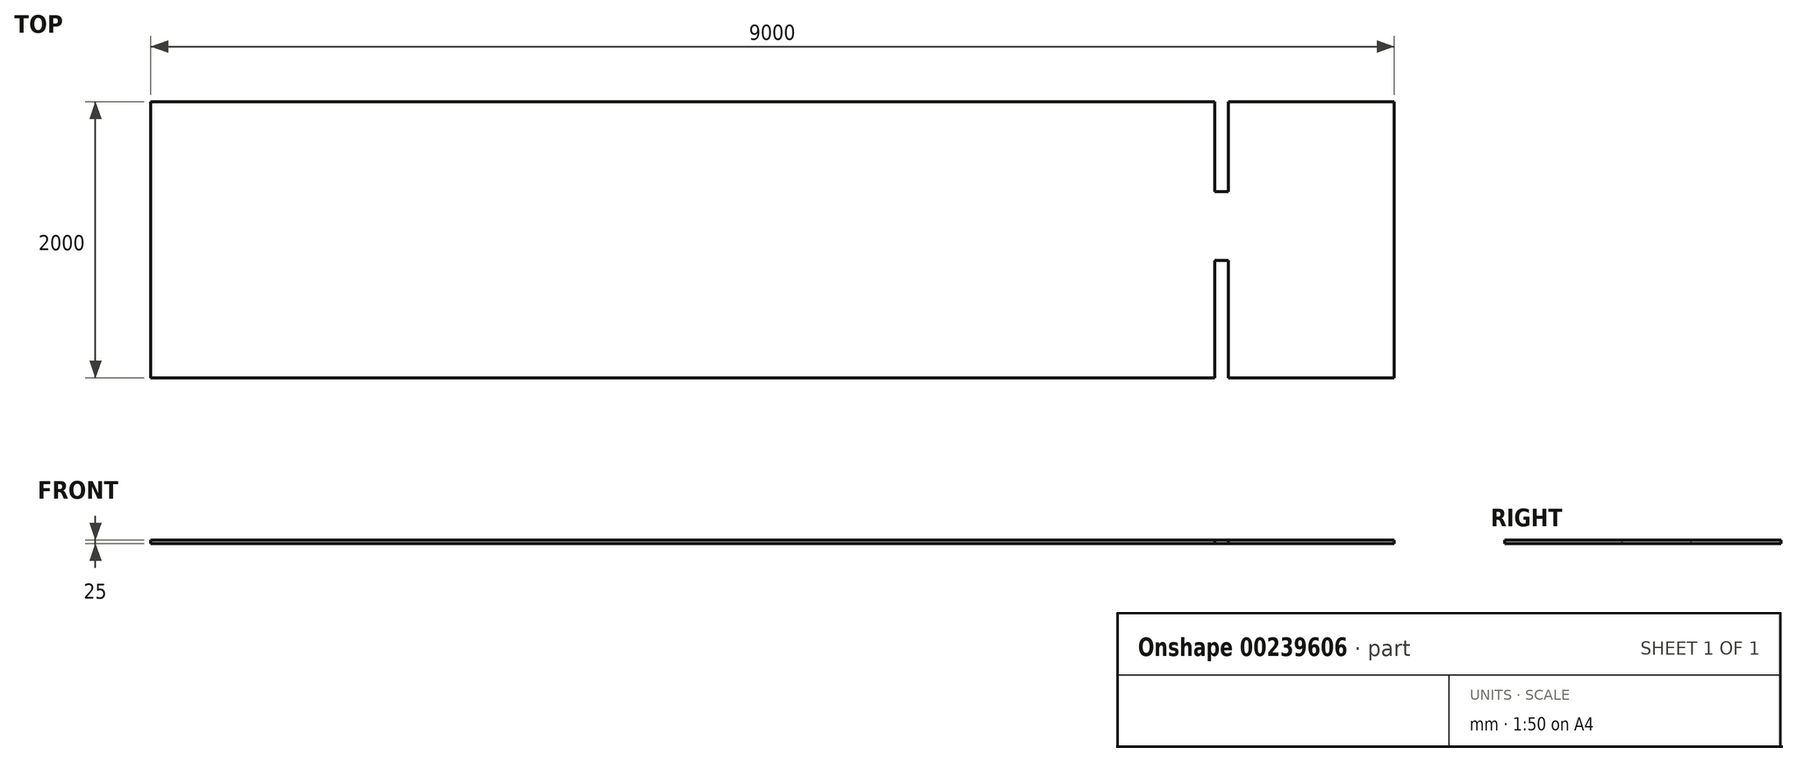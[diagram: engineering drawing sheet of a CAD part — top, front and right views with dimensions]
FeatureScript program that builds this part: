
annotation { "Feature Type Name" : "Feature", "Feature Type Description" : "" }
export const myFeature = defineFeature(function(context is Context, id is Id, definition is map)
    precondition{}
    {
        {
            var Q0;
            Q0=qCreatedBy(makeId("Top.planeOp"),FACE);
            var sketch = newSketch(context, id + "F0", { "sketchPlane" : qUnion([Q0])});
            skLineSegment(sketch, "E0.bottom", {"start": v(0, 0) * mm, "end": v(9000, 0) * mm});
            skLineSegment(sketch, "E0.top", {"start": v(0, 2000) * mm, "end": v(9000, 2000) * mm});
            skLineSegment(sketch, "E0.left", {"start": v(0, 0) * mm, "end": v(0, 2000) * mm});
            skLineSegment(sketch, "E0.right", {"start": v(9000, 0) * mm, "end": v(9000, 2000) * mm});
            skSolve(sketch);
        }
        {
            var Q0;
            Q0=makeQuery(id+"F0.imprint","IMPRINT",FACE,{"disambiguationData":[TD([[makeQuery(id+"F0.imprint","IMPRINT",EDGE,{"derivedFrom":sQuery(id+"F0.wireOp",EDGE,"E0.bottom")}),1.0]])]});
            extrude(context, id + "F1", {"entities" : qUnion([Q0]), "depth" : 25 * mm});
        }
        {
            var Q0;
            Q0=makeQuery(id+"F1.opExtrude","CAP_FACE",FACE,{"disambiguationData":[OSD([sQuery(id+"F0.wireOp",EDGE,"E0.bottom"),sQuery(id+"F0.wireOp",EDGE,"E0.top"),sQuery(id+"F0.wireOp",EDGE,"E0.left"),sQuery(id+"F0.wireOp",EDGE,"E0.right")])],"isStart":false});
            var sketch = newSketch(context, id + "F2", { "sketchPlane" : qUnion([Q0])});
            skLineSegment(sketch, "E1.bottom", {"start": v(7700, 2000) * mm, "end": v(7800, 2000) * mm});
            skLineSegment(sketch, "E1.top", {"start": v(7700, 1350) * mm, "end": v(7800, 1350) * mm});
            skLineSegment(sketch, "E1.left", {"start": v(7700, 2000) * mm, "end": v(7700, 1350) * mm});
            skLineSegment(sketch, "E1.right", {"start": v(7800, 2000) * mm, "end": v(7800, 1350) * mm});
            skLineSegment(sketch, "E2.bottom", {"start": v(7700, 0) * mm, "end": v(7800, 0) * mm});
            skLineSegment(sketch, "E2.top", {"start": v(7700, 850) * mm, "end": v(7800, 850) * mm});
            skLineSegment(sketch, "E2.left", {"start": v(7700, 0) * mm, "end": v(7700, 850) * mm});
            skLineSegment(sketch, "E2.right", {"start": v(7800, 0) * mm, "end": v(7800, 850) * mm});
            skSolve(sketch);
        }
        {
            var Q0;
            Q0 = qSketchRegion(id + "F2", true);
            extrude(context, id + "F3", {"entities" : qUnion([Q0]), "operationType" : NewBodyOperationType.REMOVE, "endBound" : BoundingType.THROUGH_ALL, "oppositeDirection" : true, "depth" : 10 * mm});
        }
    });
